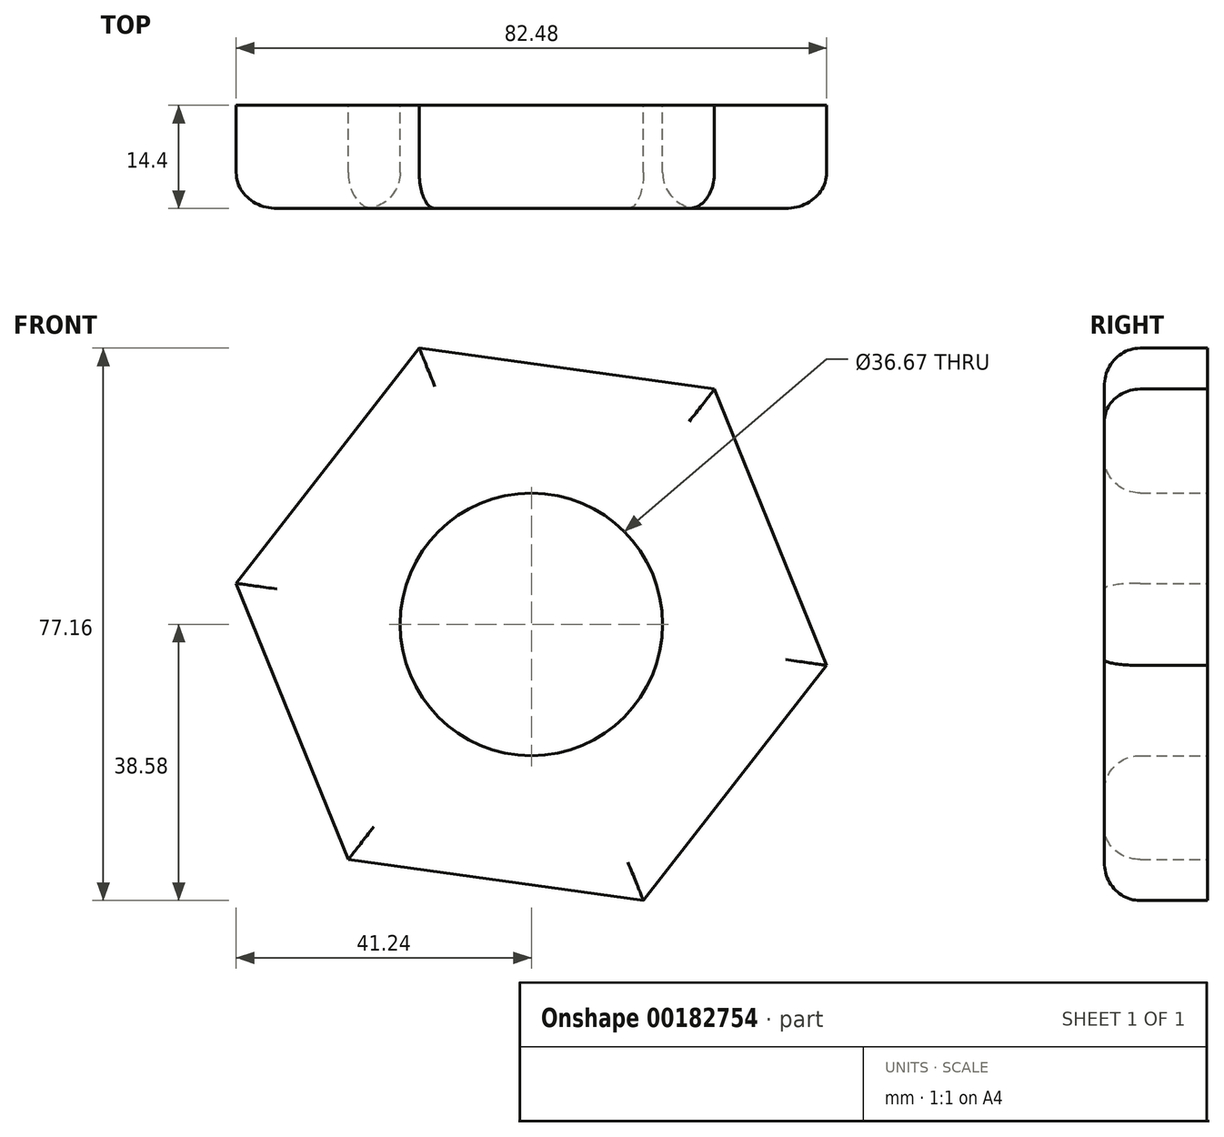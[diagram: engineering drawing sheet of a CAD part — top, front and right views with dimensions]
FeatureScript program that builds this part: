
annotation { "Feature Type Name" : "Feature", "Feature Type Description" : "" }
export const myFeature = defineFeature(function(context is Context, id is Id, definition is map)
    precondition{}
    {
        {
            var Q0;
            Q0=qCreatedBy(makeId("Front.planeOp"),FACE);
            var sketch = newSketch(context, id + "F0", { "sketchPlane" : qUnion([Q0])});
            skCircle(sketch, "E0.cCircle", {"center": v(0, 0) * mm, "radius": 36.06 * mm, "construction": true});
            skLineSegment(sketch, "E0.0", {"start": v(-25.58, -32.85) * mm, "end": v(-41.24, 5.73) * mm});
            skLineSegment(sketch, "E0.1", {"start": v(-41.24, 5.73) * mm, "end": v(-15.66, 38.58) * mm});
            skLineSegment(sketch, "E0.2", {"start": v(-15.66, 38.58) * mm, "end": v(25.58, 32.85) * mm});
            skLineSegment(sketch, "E0.3", {"start": v(25.58, 32.85) * mm, "end": v(41.24, -5.73) * mm});
            skLineSegment(sketch, "E0.4", {"start": v(41.24, -5.73) * mm, "end": v(15.66, -38.58) * mm});
            skLineSegment(sketch, "E0.5", {"start": v(15.66, -38.58) * mm, "end": v(-25.58, -32.85) * mm});
            skPoint(sketch, "E0.0.midPoint", {"position": v(-33.4, -13.56) * mm});
            skCircle(sketch, "E1", {"center": v(0, 0) * mm, "radius": 18.33 * mm});
            skSolve(sketch);
        }
        {
            var Q0;
            Q0 = qSketchRegion(id + "F0", true);
            extrude(context, id + "F1", {"entities" : qUnion([Q0]), "depth" : 14.4 * mm});
        }
        {
            var Q0;
            Q0=makeQuery(id+"F1.opExtrude","CAP_EDGE",EDGE,{"disambiguationData":[OSD([sQuery(id+"F0.wireOp",EDGE,"E1")])],"isStart":false});
            var Q1;
            Q1=makeQuery(id+"F1.opExtrude","CAP_EDGE",EDGE,{"disambiguationData":[OSD([sQuery(id+"F0.wireOp",EDGE,"E0.4")])],"isStart":false});
            var Q2;
            Q2=makeQuery(id+"F1.opExtrude","CAP_EDGE",EDGE,{"disambiguationData":[OSD([sQuery(id+"F0.wireOp",EDGE,"E0.3")])],"isStart":false});
            var Q3;
            Q3=makeQuery(id+"F1.opExtrude","CAP_EDGE",EDGE,{"disambiguationData":[OSD([sQuery(id+"F0.wireOp",EDGE,"E0.2")])],"isStart":false});
            var Q4;
            Q4=makeQuery(id+"F1.opExtrude","CAP_EDGE",EDGE,{"disambiguationData":[OSD([sQuery(id+"F0.wireOp",EDGE,"E0.1")])],"isStart":false});
            var Q5;
            Q5=makeQuery(id+"F1.opExtrude","CAP_EDGE",EDGE,{"disambiguationData":[OSD([sQuery(id+"F0.wireOp",EDGE,"E0.0")])],"isStart":false});
            var Q6;
            Q6=makeQuery(id+"F1.opExtrude","CAP_EDGE",EDGE,{"disambiguationData":[OSD([sQuery(id+"F0.wireOp",EDGE,"E0.5")])],"isStart":false});
            fillet(context, id + "F2", {"entities" : qUnion([Q0, Q1, Q2, Q3, Q4, Q5, Q6]), "radius" : 5 * mm, "tangentPropagation" : true, "allowEdgeOverflow" : false});
        }
    });
